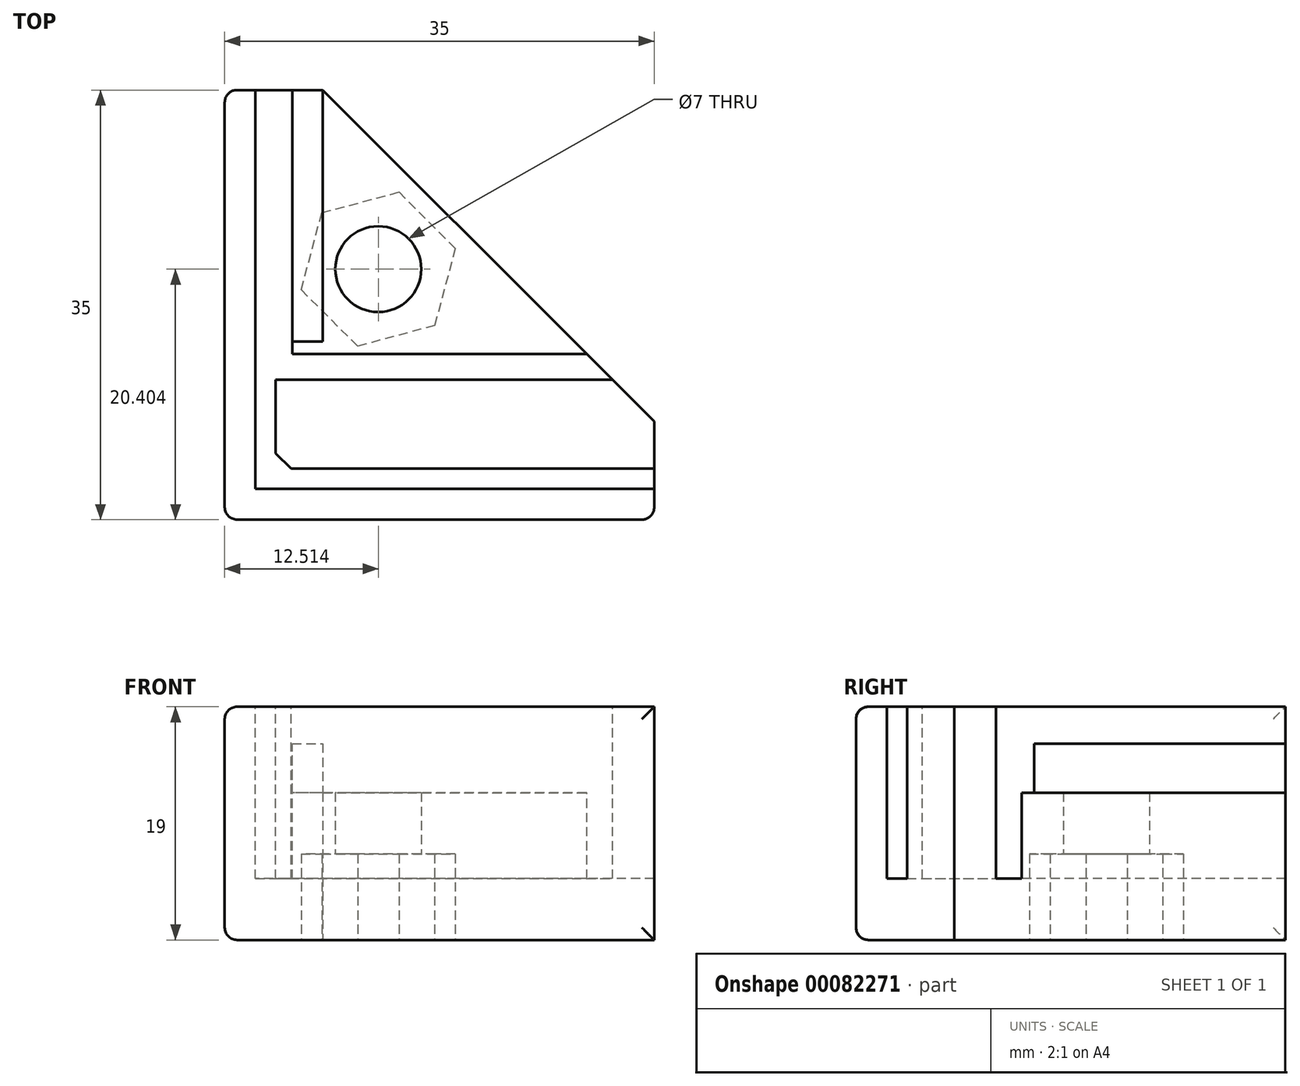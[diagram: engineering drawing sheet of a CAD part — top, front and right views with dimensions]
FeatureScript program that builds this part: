
annotation { "Feature Type Name" : "Feature", "Feature Type Description" : "" }
export const myFeature = defineFeature(function(context is Context, id is Id, definition is map)
    precondition{}
    {
        {
            var Q0;
            Q0=qCreatedBy(makeId("Top.planeOp"),FACE);
            var sketch = newSketch(context, id + "F0", { "sketchPlane" : qUnion([Q0])});
            skLineSegment(sketch, "E0", {"start": v(0, 0) * mm, "end": v(0, 35) * mm});
            skLineSegment(sketch, "E1", {"start": v(0, 35) * mm, "end": v(8, 35) * mm});
            skLineSegment(sketch, "E2", {"start": v(8, 35) * mm, "end": v(35, 8) * mm});
            skLineSegment(sketch, "E3", {"start": v(35, 8) * mm, "end": v(35, 0) * mm});
            skLineSegment(sketch, "E4", {"start": v(35, 0) * mm, "end": v(0, 0) * mm});
            skSolve(sketch);
        }
        {
            var Q0;
            Q0=makeQuery(id+"F0.imprint","IMPRINT",FACE,{"disambiguationData":[TD([[makeQuery(id+"F0.imprint","IMPRINT",EDGE,{"derivedFrom":sQuery(id+"F0.wireOp",EDGE,"E0")}),-1.0]])]});
            extrude(context, id + "F1", {"entities" : qUnion([Q0]), "depth" : 19 * mm});
        }
        {
            var Q0;
            Q0=makeQuery(id+"F1.opExtrude","CAP_FACE",FACE,{"disambiguationData":[OSD([sQuery(id+"F0.wireOp",EDGE,"E0"),sQuery(id+"F0.wireOp",EDGE,"E1"),sQuery(id+"F0.wireOp",EDGE,"E2"),sQuery(id+"F0.wireOp",EDGE,"E3"),sQuery(id+"F0.wireOp",EDGE,"E4"),sQuery(id+"F0.wireOp",EDGE,"FbcIN14l-oaw5-KCrL-uuZt-MgXA5B638lM7")])],"isStart":false});
            var sketch = newSketch(context, id + "F2", { "sketchPlane" : qUnion([Q0])});
            skLineSegment(sketch, "E5", {"start": v(35, 0) * mm, "end": v(35, 2.5) * mm});
            skLineSegment(sketch, "E6", {"start": v(35, 2.5) * mm, "end": v(2.5, 2.5) * mm});
            skLineSegment(sketch, "E7", {"start": v(2.5, 2.5) * mm, "end": v(2.5, 35) * mm});
            skLineSegment(sketch, "E8", {"start": v(2.5, 35) * mm, "end": v(0, 35) * mm});
            skLineSegment(sketch, "E9", {"start": v(0, 35) * mm, "end": v(0, 0) * mm});
            skLineSegment(sketch, "E10", {"start": v(0, 0) * mm, "end": v(35, 0) * mm});
            skLineSegment(sketch, "E11", {"start": v(35, 2.5) * mm, "end": v(35, 4.15) * mm});
            skLineSegment(sketch, "E12", {"start": v(35, 4.15) * mm, "end": v(5.4, 4.15) * mm});
            skLineSegment(sketch, "E13", {"start": v(35, 4.15) * mm, "end": v(35, 8) * mm});
            skLineSegment(sketch, "E14", {"start": v(2.5, 35) * mm, "end": v(5.5, 35) * mm});
            skLineSegment(sketch, "E15", {"start": v(5.5, 35) * mm, "end": v(5.5, 11.4) * mm});
            skLineSegment(sketch, "E16", {"start": v(4.15, 5.4) * mm, "end": v(4.15, 11.4) * mm});
            skLineSegment(sketch, "E17", {"start": v(5.5, 35) * mm, "end": v(8, 35) * mm});
            skLineSegment(sketch, "E18", {"start": v(8, 35) * mm, "end": v(8, 14.5) * mm});
            skLineSegment(sketch, "E19", {"start": v(8, 14.5) * mm, "end": v(5.5, 14.5) * mm});
            skLineSegment(sketch, "E20", {"start": v(4.15, 11.4) * mm, "end": v(31.6, 11.4) * mm});
            skLineSegment(sketch, "E21", {"start": v(31.6, 11.4) * mm, "end": v(29.5, 13.5) * mm});
            skLineSegment(sketch, "E22", {"start": v(29.5, 13.5) * mm, "end": v(5.5, 13.5) * mm});
            skLineSegment(sketch, "E23", {"start": v(5.4, 4.15) * mm, "end": v(4.15, 5.4) * mm});
            skPoint(sketch, "E24.orphan", {"position": v(4.15, 4.15) * mm});
            skSolve(sketch);
        }
        {
            var Q0;
            Q0=makeQuery(id+"F2.imprint","IMPRINT",FACE,{"disambiguationData":[TD([[makeQuery(id+"F2.imprint","IMPRINT",EDGE,{"derivedFrom":sQuery(id+"F2.wireOp",EDGE,"E6")}),-1.0]])]});
            extrude(context, id + "F3", {"entities" : qUnion([Q0]), "operationType" : NewBodyOperationType.REMOVE, "oppositeDirection" : true, "depth" : 14 * mm});
        }
        {
            var Q0;
            Q0=makeQuery(id+"F0.imprint","IMPRINT",FACE,{"disambiguationData":[TD([[makeQuery(id+"F0.imprint","IMPRINT",EDGE,{"derivedFrom":sQuery(id+"F0.wireOp",EDGE,"E0")}),-1.0]])]});
            var sketch = newSketch(context, id + "F4", { "sketchPlane" : qUnion([Q0])});
            skLineSegment(sketch, "E25", {"start": v(0, 0) * mm, "end": v(0, 35) * mm});
            skLineSegment(sketch, "E26", {"start": v(0, 35) * mm, "end": v(8, 35) * mm});
            skLineSegment(sketch, "E27", {"start": v(8, 35) * mm, "end": v(35, 8) * mm});
            skLineSegment(sketch, "E28", {"start": v(35, 8) * mm, "end": v(35, 0) * mm});
            skLineSegment(sketch, "E29", {"start": v(35, 0) * mm, "end": v(0, 0) * mm});
            skLineSegment(sketch, "E30", {"start": v(14.2, 26.68) * mm, "end": v(18.8, 22.09) * mm});
            skLineSegment(sketch, "E31", {"start": v(18.8, 22.09) * mm, "end": v(17.1, 15.8) * mm});
            skLineSegment(sketch, "E32", {"start": v(17.1, 15.8) * mm, "end": v(10.83, 14.13) * mm});
            skLineSegment(sketch, "E33", {"start": v(10.83, 14.13) * mm, "end": v(6.24, 18.72) * mm});
            skLineSegment(sketch, "E34", {"start": v(6.24, 18.72) * mm, "end": v(7.92, 25) * mm});
            skLineSegment(sketch, "E35", {"start": v(7.92, 25) * mm, "end": v(14.2, 26.68) * mm});
            skCircle(sketch, "E36", {"center": v(12.51, 20.4) * mm, "radius": 3.5 * mm});
            skLineSegment(sketch, "E37", {"start": v(7.92, 25) * mm, "end": v(8, 35) * mm, "construction": true});
            skLineSegment(sketch, "E38", {"start": v(12.51, 20.4) * mm, "end": v(6.24, 18.72) * mm, "construction": true});
            skLineSegment(sketch, "E39", {"start": v(12.51, 20.4) * mm, "end": v(7.92, 25) * mm, "construction": true});
            skLineSegment(sketch, "E40", {"start": v(12.51, 20.4) * mm, "end": v(17.1, 15.8) * mm, "construction": true});
            skSolve(sketch);
        }
        {
            var Q0;
            Q0=makeQuery(id+"F4.imprint","IMPRINT",FACE,{"disambiguationData":[TD([[makeQuery(id+"F4.imprint","IMPRINT",EDGE,{"derivedFrom":sQuery(id+"F4.wireOp",EDGE,"E30")}),-1.0]])]});
            extrude(context, id + "F5", {"entities" : qUnion([Q0]), "operationType" : NewBodyOperationType.REMOVE, "depth" : 7 * mm});
        }
        {
            var Q0;
            Q0=makeQuery(id+"F2.imprint","IMPRINT",FACE,{"disambiguationData":[TD([[makeQuery(id+"F2.imprint","IMPRINT",EDGE,{"derivedFrom":sQuery(id+"F2.wireOp",EDGE,"E18")}),1.0]])]});
            extrude(context, id + "F6", {"entities" : qUnion([Q0]), "operationType" : NewBodyOperationType.REMOVE, "oppositeDirection" : true, "depth" : 7 * mm});
        }
        {
            var Q0;
            Q0=makeQuery(id+"F4.imprint","IMPRINT",FACE,{"disambiguationData":[TD([[makeQuery(id+"F4.imprint","IMPRINT",EDGE,{"derivedFrom":sQuery(id+"F4.wireOp",EDGE,"E36")}),1.0]])]});
            extrude(context, id + "F7", {"entities" : qUnion([Q0]), "operationType" : NewBodyOperationType.REMOVE, "depth" : 25 * mm});
        }
        {
            var Q0;
            {var subQ0=sQuery(id+"F2.wireOp",EDGE,"E20");Q0=makeQuery(id+"F2.imprint","IMPRINT",FACE,{"disambiguationData":[TD([[makeQuery(id+"F2.imprint","IMPRINT",EDGE,{"derivedFrom":subQ0}),1.0]])]});}
            extrude(context, id + "F8", {"entities" : qUnion([Q0]), "operationType" : NewBodyOperationType.REMOVE, "oppositeDirection" : true, "depth" : 14 * mm});
        }
        {
            var Q0;
            Q0=makeQuery(id+"F1.opExtrude","SWEPT_FACE",FACE,{"disambiguationData":[OSD([sQuery(id+"F0.wireOp",EDGE,"E0")])]});
            var Q1;
            Q1=makeQuery(id+"F1.opExtrude","SWEPT_FACE",FACE,{"disambiguationData":[OSD([sQuery(id+"F0.wireOp",EDGE,"E4")])]});
            fillet(context, id + "F9", {"entities" : qUnion([Q0, Q1]), "radius" : 1 * mm, "tangentPropagation" : true, "allowEdgeOverflow" : false});
        }
        {
            var Q0;
            {var subQ0=sQuery(id+"F2.wireOp",EDGE,"E17");Q0=makeQuery(id+"F2.imprint","IMPRINT",FACE,{"disambiguationData":[TD([[makeQuery(id+"F2.imprint","IMPRINT",EDGE,{"derivedFrom":subQ0}),-1.0]])]});}
            extrude(context, id + "F10", {"entities" : qUnion([Q0]), "operationType" : NewBodyOperationType.REMOVE, "oppositeDirection" : true, "depth" : 3 * mm});
        }
    });
